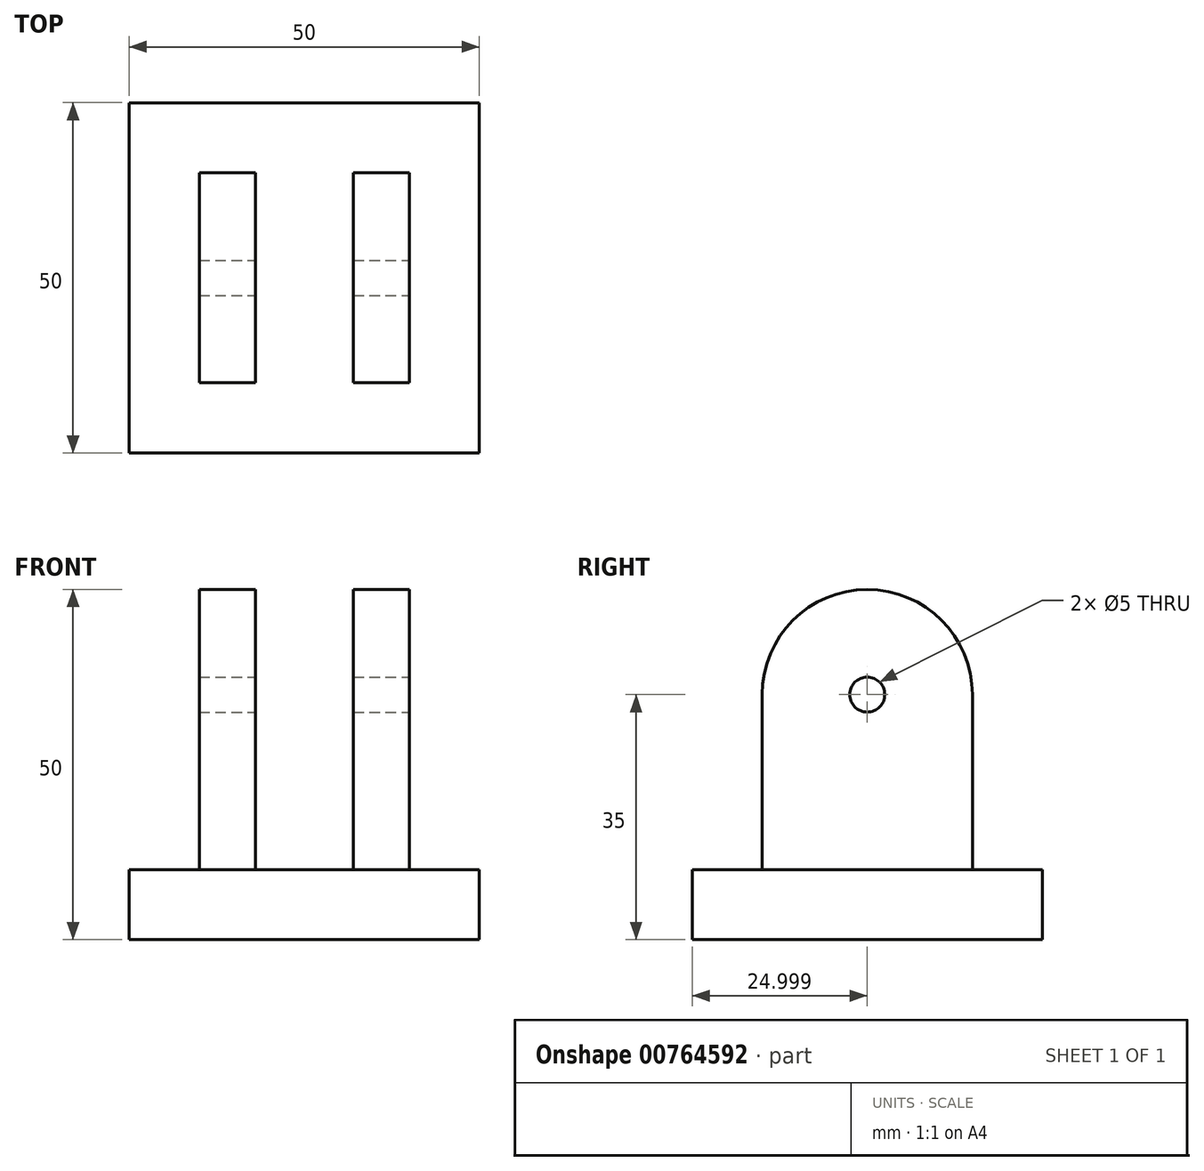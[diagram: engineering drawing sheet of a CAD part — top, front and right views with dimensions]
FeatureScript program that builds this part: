
annotation { "Feature Type Name" : "Feature", "Feature Type Description" : "" }
export const myFeature = defineFeature(function(context is Context, id is Id, definition is map)
    precondition{}
    {
        {
            var Q0;
            Q0=qCreatedBy(makeId("Top.planeOp"),FACE);
            var sketch = newSketch(context, id + "F0", { "sketchPlane" : qUnion([Q0])});
            skLineSegment(sketch, "E0.bottom", {"start": v(-22.7, 23.26) * mm, "end": v(27.3, 23.26) * mm});
            skLineSegment(sketch, "E0.top", {"start": v(-22.7, -26.74) * mm, "end": v(27.3, -26.74) * mm});
            skLineSegment(sketch, "E0.left", {"start": v(-22.7, 23.26) * mm, "end": v(-22.7, -26.74) * mm});
            skLineSegment(sketch, "E0.right", {"start": v(27.3, 23.26) * mm, "end": v(27.3, -26.74) * mm});
            skSolve(sketch);
        }
        {
            var Q0;
            Q0=makeQuery(id+"F0.imprint","IMPRINT",FACE,{"disambiguationData":[TD([[makeQuery(id+"F0.imprint","IMPRINT",EDGE,{"derivedFrom":sQuery(id+"F0.wireOp",EDGE,"E0.bottom")}),-1.0]])]});
            extrude(context, id + "F1", {"entities" : qUnion([Q0]), "depth" : 10 * mm, "offsetDistance" : 25 * mm});
        }
        {
            var Q0;
            Q0=makeQuery(id+"F1.opExtrude","CAP_FACE",FACE,{"disambiguationData":[OSD([sQuery(id+"F0.wireOp",EDGE,"E0.bottom"),sQuery(id+"F0.wireOp",EDGE,"E0.top"),sQuery(id+"F0.wireOp",EDGE,"E0.left"),sQuery(id+"F0.wireOp",EDGE,"E0.right")])],"isStart":false});
            var sketch = newSketch(context, id + "F2", { "sketchPlane" : qUnion([Q0])});
            skLineSegment(sketch, "E1.bottom", {"start": v(-12.7, 13.26) * mm, "end": v(-4.65, 13.26) * mm});
            skLineSegment(sketch, "E1.top", {"start": v(-12.7, -16.74) * mm, "end": v(-4.65, -16.74) * mm});
            skLineSegment(sketch, "E1.left", {"start": v(-12.7, 13.26) * mm, "end": v(-12.7, -16.74) * mm});
            skLineSegment(sketch, "E1.right", {"start": v(-4.65, 13.26) * mm, "end": v(-4.65, -16.74) * mm});
            skLineSegment(sketch, "E2.bottom", {"start": v(9.3, 13.26) * mm, "end": v(17.3, 13.26) * mm});
            skLineSegment(sketch, "E2.top", {"start": v(9.3, -16.74) * mm, "end": v(17.3, -16.74) * mm});
            skLineSegment(sketch, "E2.left", {"start": v(9.3, 13.26) * mm, "end": v(9.3, -16.74) * mm});
            skLineSegment(sketch, "E2.right", {"start": v(17.3, 13.26) * mm, "end": v(17.3, -16.74) * mm});
            skSolve(sketch);
        }
        {
            var Q0;
            Q0=makeQuery(id+"F2.imprint","IMPRINT",FACE,{"disambiguationData":[TD([[makeQuery(id+"F2.imprint","IMPRINT",EDGE,{"derivedFrom":sQuery(id+"F2.wireOp",EDGE,"E1.bottom")}),-1.0]])]});
            var Q1;
            Q1=makeQuery(id+"F2.imprint","IMPRINT",FACE,{"disambiguationData":[TD([[makeQuery(id+"F2.imprint","IMPRINT",EDGE,{"derivedFrom":sQuery(id+"F2.wireOp",EDGE,"E2.bottom")}),-1.0]])]});
            extrude(context, id + "F3", {"entities" : qUnion([Q0, Q1]), "operationType" : NewBodyOperationType.ADD, "depth" : 40 * mm, "offsetDistance" : 25 * mm});
        }
        {
            var Q0;
            Q0=makeQuery(id+"F3.opExtrude","CAP_EDGE",EDGE,{"disambiguationData":[OSD([sQuery(id+"F2.wireOp",EDGE,"E1.top")])],"isStart":false});
            var Q1;
            Q1=makeQuery(id+"F3.opExtrude","CAP_EDGE",EDGE,{"disambiguationData":[OSD([sQuery(id+"F2.wireOp",EDGE,"E2.top")])],"isStart":false});
            var Q2;
            Q2=makeQuery(id+"F3.opExtrude","CAP_EDGE",EDGE,{"disambiguationData":[OSD([sQuery(id+"F2.wireOp",EDGE,"E1.bottom")])],"isStart":false});
            var Q3;
            Q3=makeQuery(id+"F3.opExtrude","CAP_EDGE",EDGE,{"disambiguationData":[OSD([sQuery(id+"F2.wireOp",EDGE,"E2.bottom")])],"isStart":false});
            fillet(context, id + "F4", {"entities" : qUnion([Q0, Q1, Q2, Q3]), "radius" : 15 * mm, "tangentPropagation" : true, "allowEdgeOverflow" : false});
        }
        {
            var Q0;
            Q0=makeQuery(id+"F3.opExtrude","SWEPT_FACE",FACE,{"disambiguationData":[OSD([sQuery(id+"F2.wireOp",EDGE,"E2.right")])]});
            var sketch = newSketch(context, id + "F5", { "sketchPlane" : qUnion([Q0])});
            skPoint(sketch, "E3", {"position": v(-1.74, 35) * mm});
            skSolve(sketch);
        }
        {
            var Q0;
            Q0=sQuery(id+"F5.wireOp",VERTEX,"E3");
            var Q1;
            Q1=makeQuery(id+"F1.opExtrude","SWEPT_BODY",BODY,{"disambiguationData":[OSD([sQuery(id+"F0.wireOp",EDGE,"E0.bottom"),sQuery(id+"F0.wireOp",EDGE,"E0.top"),sQuery(id+"F0.wireOp",EDGE,"E0.left"),sQuery(id+"F0.wireOp",EDGE,"E0.right")])]});
            hole(context, id + "F6", {"style" : HoleStyle.SIMPLE, "endStyle" : HoleEndStyle.THROUGH, "holeDiameter" : 5 * mm, "majorDiameter" : 5 * mm, "isTappedThrough" : true, "tappedDepth" : 12 * mm, "tapClearance" : 3, "locations" : qUnion([Q0]), "scope" : qUnion([Q1])});
        }
    });
